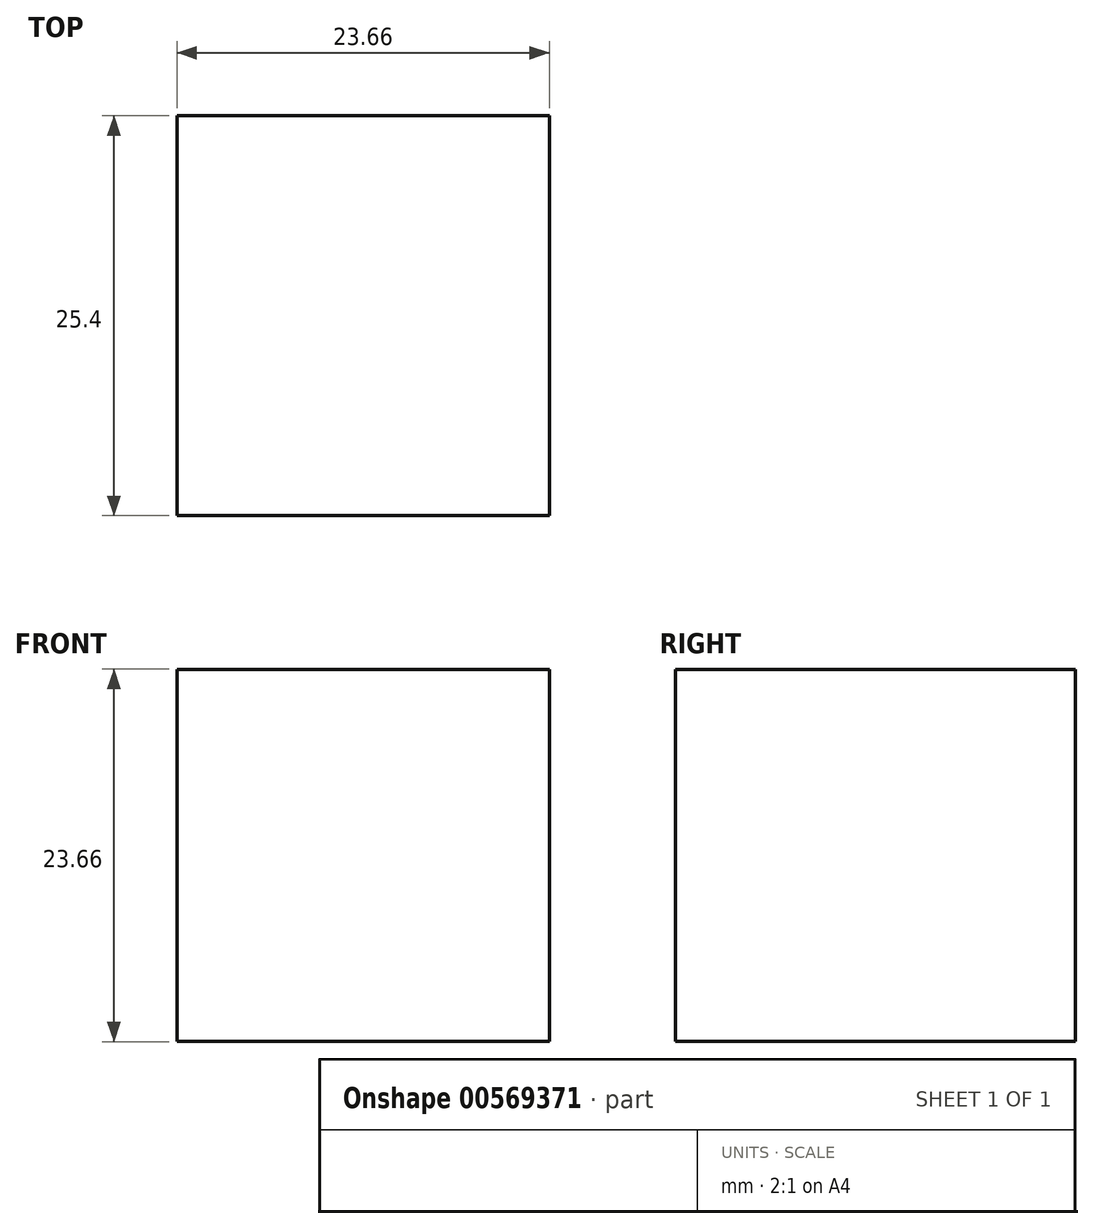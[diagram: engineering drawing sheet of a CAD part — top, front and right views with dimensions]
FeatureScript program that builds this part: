
annotation { "Feature Type Name" : "Feature", "Feature Type Description" : "" }
export const myFeature = defineFeature(function(context is Context, id is Id, definition is map)
    precondition{}
    {
        {
            var Q0;
            Q0=qCreatedBy(makeId("Front.planeOp"),FACE);
            var sketch = newSketch(context, id + "F0", { "sketchPlane" : qUnion([Q0])});
            skLineSegment(sketch, "E0.bottom", {"start": v(-11.82, 11.82) * mm, "end": v(11.83, 11.82) * mm});
            skLineSegment(sketch, "E0.top", {"start": v(-11.83, -11.82) * mm, "end": v(11.82, -11.82) * mm});
            skLineSegment(sketch, "E0.left", {"start": v(-11.82, 11.82) * mm, "end": v(-11.83, -11.82) * mm});
            skLineSegment(sketch, "E0.right", {"start": v(11.83, 11.82) * mm, "end": v(11.82, -11.82) * mm});
            skPoint(sketch, "E0.middle", {"position": v(0, 0) * mm});
            skSolve(sketch);
        }
        {
            var Q0;
            Q0 = qSketchRegion(id + "F0", true);
            extrude(context, id + "F1", {"entities" : qUnion([Q0]), "endBound" : BoundingType.SYMMETRIC, "depth" : 25.4 * mm, "offsetDistance" : 25.4 * mm});
        }
    });
